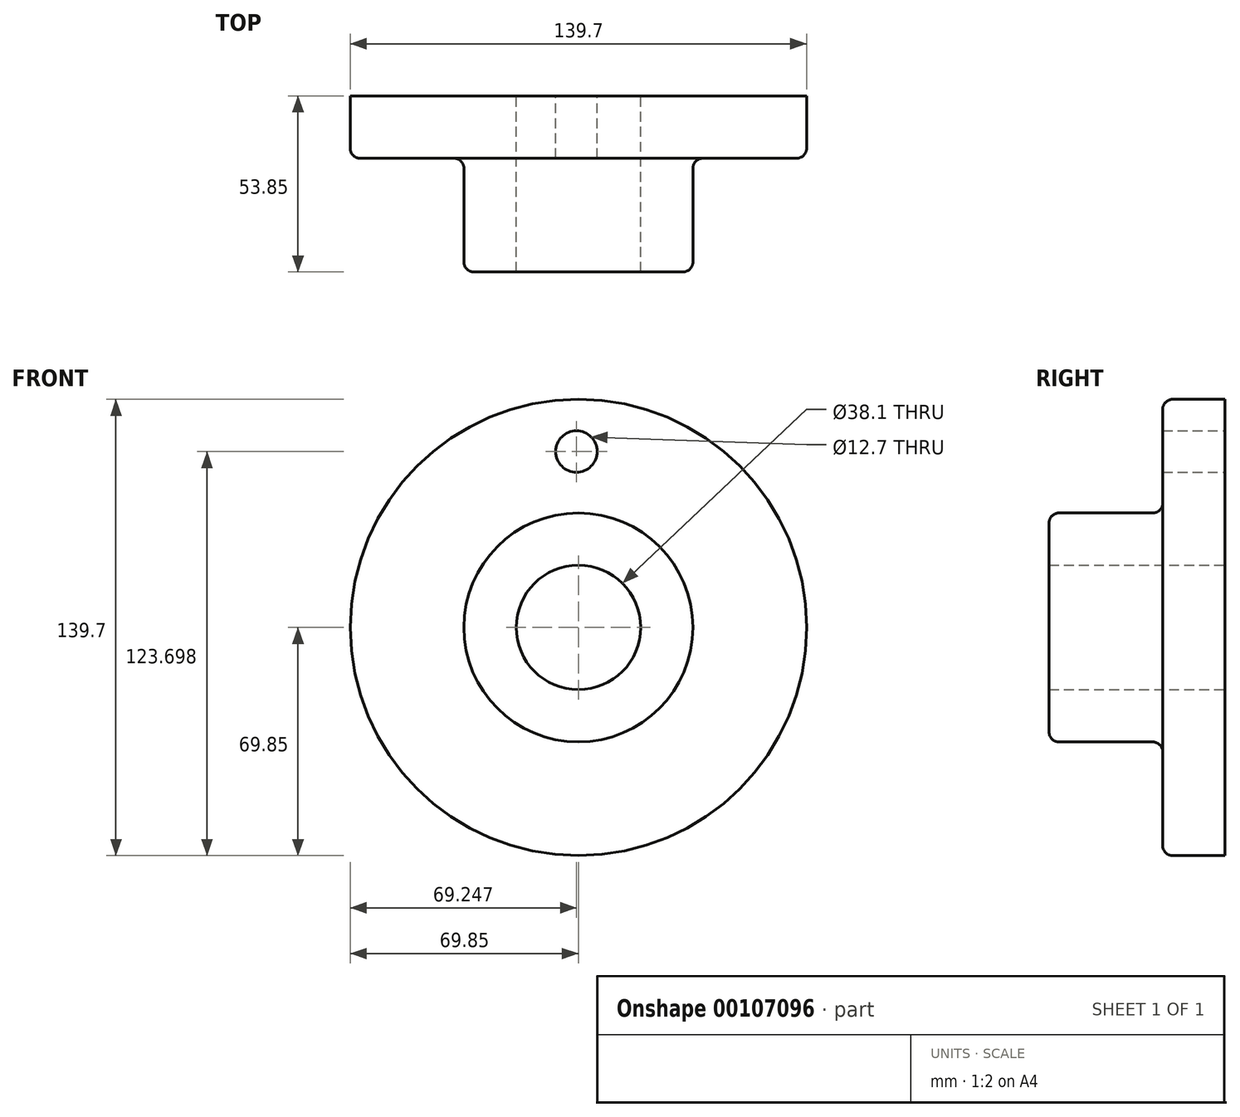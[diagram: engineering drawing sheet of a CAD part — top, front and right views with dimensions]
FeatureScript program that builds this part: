
annotation { "Feature Type Name" : "Feature", "Feature Type Description" : "" }
export const myFeature = defineFeature(function(context is Context, id is Id, definition is map)
    precondition{}
    {
        {
            var Q0;
            Q0=qCreatedBy(makeId("Top.planeOp"),FACE);
            var sketch = newSketch(context, id + "F0", { "sketchPlane" : qUnion([Q0])});
            skLineSegment(sketch, "E0", {"start": v(0, 0) * mm, "end": v(0, -53.85) * mm});
            skLineSegment(sketch, "E1", {"start": v(0, -53.85) * mm, "end": v(16, -53.85) * mm});
            skLineSegment(sketch, "E2", {"start": v(16, -53.85) * mm, "end": v(16, -19.05) * mm});
            skLineSegment(sketch, "E3", {"start": v(16, -19.05) * mm, "end": v(50.8, -19.05) * mm});
            skLineSegment(sketch, "E4", {"start": v(50.8, -19.05) * mm, "end": v(50.8, 0) * mm});
            skLineSegment(sketch, "E5", {"start": v(50.8, 0) * mm, "end": v(0, 0) * mm});
            skLineSegment(sketch, "E6", {"start": v(-19.05, 0) * mm, "end": v(-19.05, -54.22) * mm, "construction": true});
            skLineSegment(sketch, "E7", {"start": v(-38.1, 0) * mm, "end": v(-38.1, -54.33) * mm, "construction": true});
            skLineSegment(sketch, "E8", {"start": v(-54.1, 0) * mm, "end": v(-54.1, -55.33) * mm, "construction": true});
            skSolve(sketch);
        }
        {
            var Q0;
            Q0=makeQuery(id+"F0.imprint","IMPRINT",FACE,{"disambiguationData":[TD([[makeQuery(id+"F0.imprint","IMPRINT",EDGE,{"derivedFrom":sQuery(id+"F0.wireOp",EDGE,"E0")}),1.0]])]});
            var Q1;
            Q1=sQuery(id+"F0.wireOp",EDGE,"E6");
            revolve(context, id + "F1", {"entities" : qUnion([Q0]), "axis" : qUnion([Q1]), "revolveType" : RevolveType.FULL});
        }
        {
            var Q0;
            Q0=qCreatedBy(makeId("Front.planeOp"),FACE);
            var sketch = newSketch(context, id + "F2", { "sketchPlane" : qUnion([Q0])});
            skCircle(sketch, "E9", {"center": v(-19.65, 53.85) * mm, "radius": 6.35 * mm});
            skCircle(sketch, "E10", {"center": v(-19.65, 0) * mm, "radius": 53.85 * mm, "construction": true});
            skSolve(sketch);
        }
        {
            var Q0;
            Q0=makeQuery(id+"F1.opRevolve","SWEPT_EDGE",EDGE,{"disambiguationData":[OSD([sQuery(id+"F0.wireOp",EDGE,"E3"),sQuery(id+"F0.wireOp",EDGE,"E4")])]});
            fillet(context, id + "F3", {"entities" : qUnion([Q0]), "radius" : 3.05 * mm, "tangentPropagation" : true, "allowEdgeOverflow" : false});
        }
        {
            var Q0;
            Q0=makeQuery(id+"F1.opRevolve","SWEPT_EDGE",EDGE,{"disambiguationData":[OSD([sQuery(id+"F0.wireOp",EDGE,"E2"),sQuery(id+"F0.wireOp",EDGE,"E3")])]});
            fillet(context, id + "F4", {"entities" : qUnion([Q0]), "radius" : 3.05 * mm, "tangentPropagation" : true, "allowEdgeOverflow" : false});
        }
        {
            var Q0;
            Q0=makeQuery(id+"F1.opRevolve","SWEPT_EDGE",EDGE,{"disambiguationData":[OSD([sQuery(id+"F0.wireOp",EDGE,"E1"),sQuery(id+"F0.wireOp",EDGE,"E2")])]});
            fillet(context, id + "F5", {"entities" : qUnion([Q0]), "radius" : 3.05 * mm, "tangentPropagation" : true, "allowEdgeOverflow" : false});
        }
        {
            var Q0;
            Q0 = qSketchRegion(id + "F2", true);
            extrude(context, id + "F6", {"entities" : qUnion([Q0]), "operationType" : NewBodyOperationType.REMOVE, "depth" : 25.4 * mm});
        }
    });
